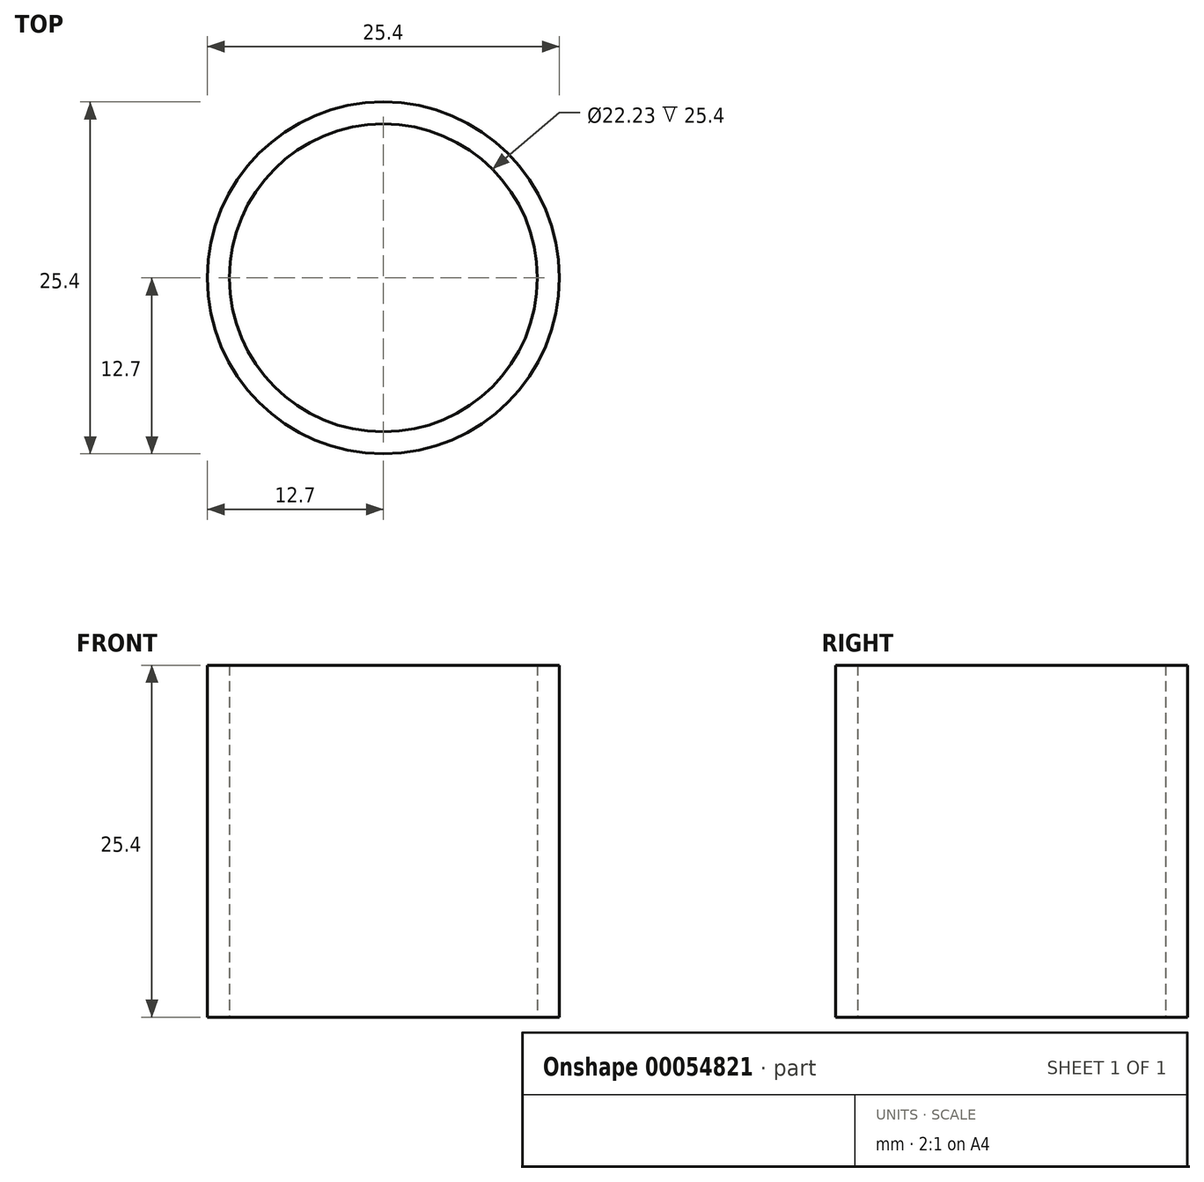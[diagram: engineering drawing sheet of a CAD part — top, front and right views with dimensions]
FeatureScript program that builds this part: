
annotation { "Feature Type Name" : "Feature", "Feature Type Description" : "" }
export const myFeature = defineFeature(function(context is Context, id is Id, definition is map)
    precondition{}
    {
        {
            var Q0;
            Q0=qCreatedBy(makeId("Top.planeOp"),FACE);
            var sketch = newSketch(context, id + "F0", { "sketchPlane" : qUnion([Q0])});
            skCircle(sketch, "E0", {"center": v(0, 0) * mm, "radius": 11.11 * mm});
            skCircle(sketch, "E1", {"center": v(0, 0) * mm, "radius": 12.7 * mm});
            skSolve(sketch);
        }
        {
            var Q0;
            Q0 = qSketchRegion(id + "F0", true);
            extrude(context, id + "F1", {"entities" : qUnion([Q0]), "depth" : 25.4 * mm});
        }
    });
